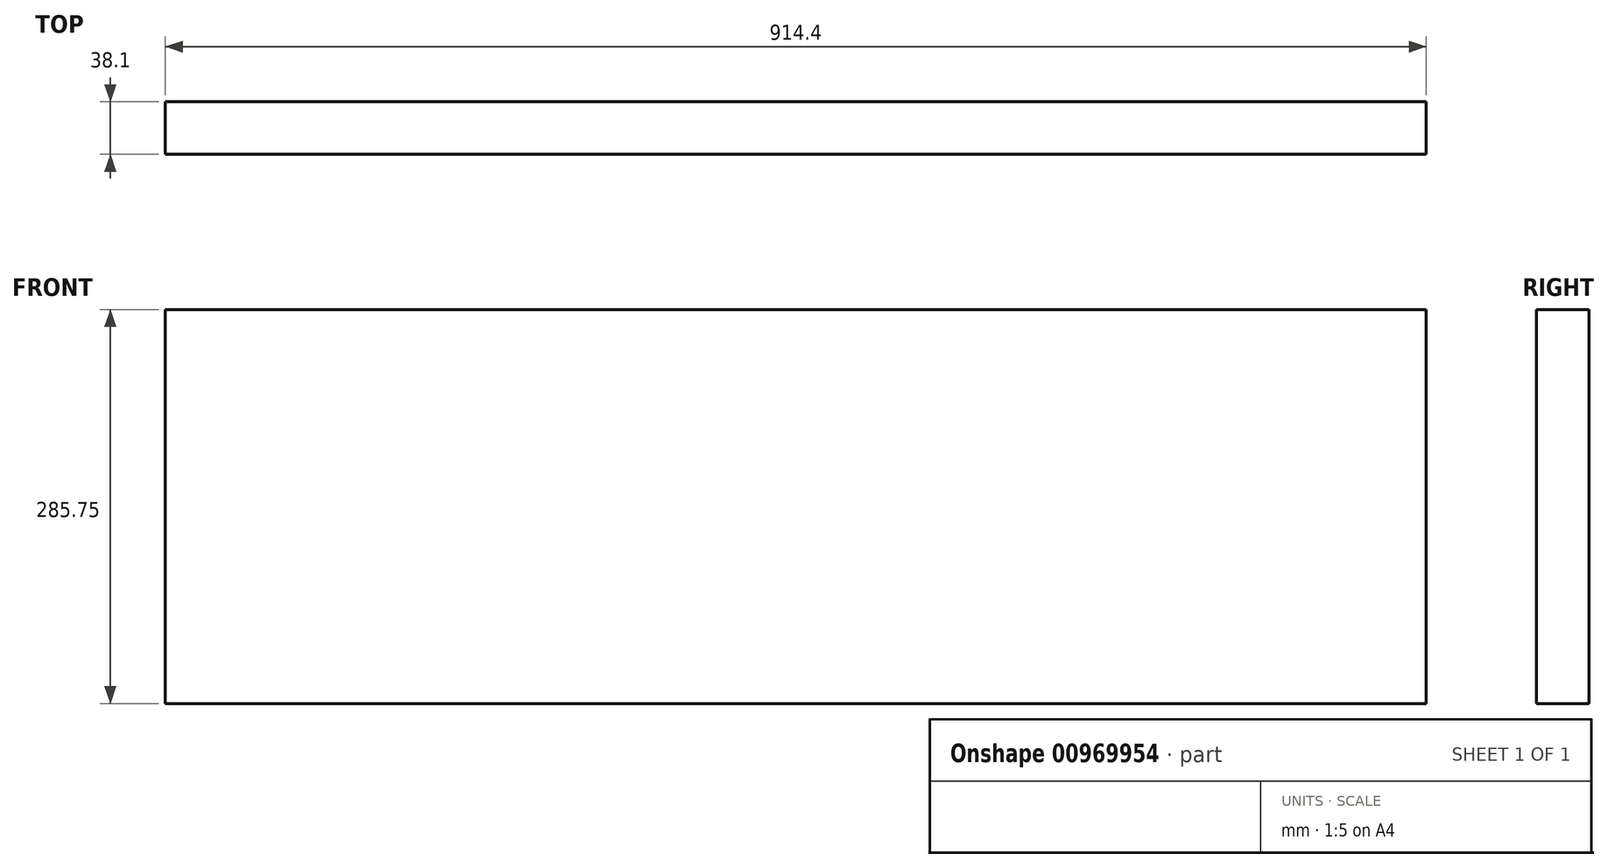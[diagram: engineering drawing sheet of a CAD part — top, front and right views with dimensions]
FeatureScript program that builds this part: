
annotation { "Feature Type Name" : "Feature", "Feature Type Description" : "" }
export const myFeature = defineFeature(function(context is Context, id is Id, definition is map)
    precondition{}
    {
        {
            var Q0;
            Q0=qCreatedBy(makeId("Top.planeOp"),FACE);
            var sketch = newSketch(context, id + "F0", { "sketchPlane" : qUnion([Q0])});
            skLineSegment(sketch, "E0.bottom", {"start": v(0, 0) * mm, "end": v(914.4, 0) * mm});
            skLineSegment(sketch, "E0.top", {"start": v(0, 38.1) * mm, "end": v(914.4, 38.1) * mm});
            skLineSegment(sketch, "E0.left", {"start": v(0, 0) * mm, "end": v(0, 38.1) * mm});
            skLineSegment(sketch, "E0.right", {"start": v(914.4, 0) * mm, "end": v(914.4, 38.1) * mm});
            skSolve(sketch);
        }
        {
            var Q0;
            Q0 = qSketchRegion(id + "F0", true);
            extrude(context, id + "F1", {"entities" : qUnion([Q0]), "flatOperationType" : FlatOperationType.REMOVE, "depth" : 285.75 * mm, "offsetDistance" : 25.4 * mm, "domain" : OperationDomain.MODEL});
        }
    });
